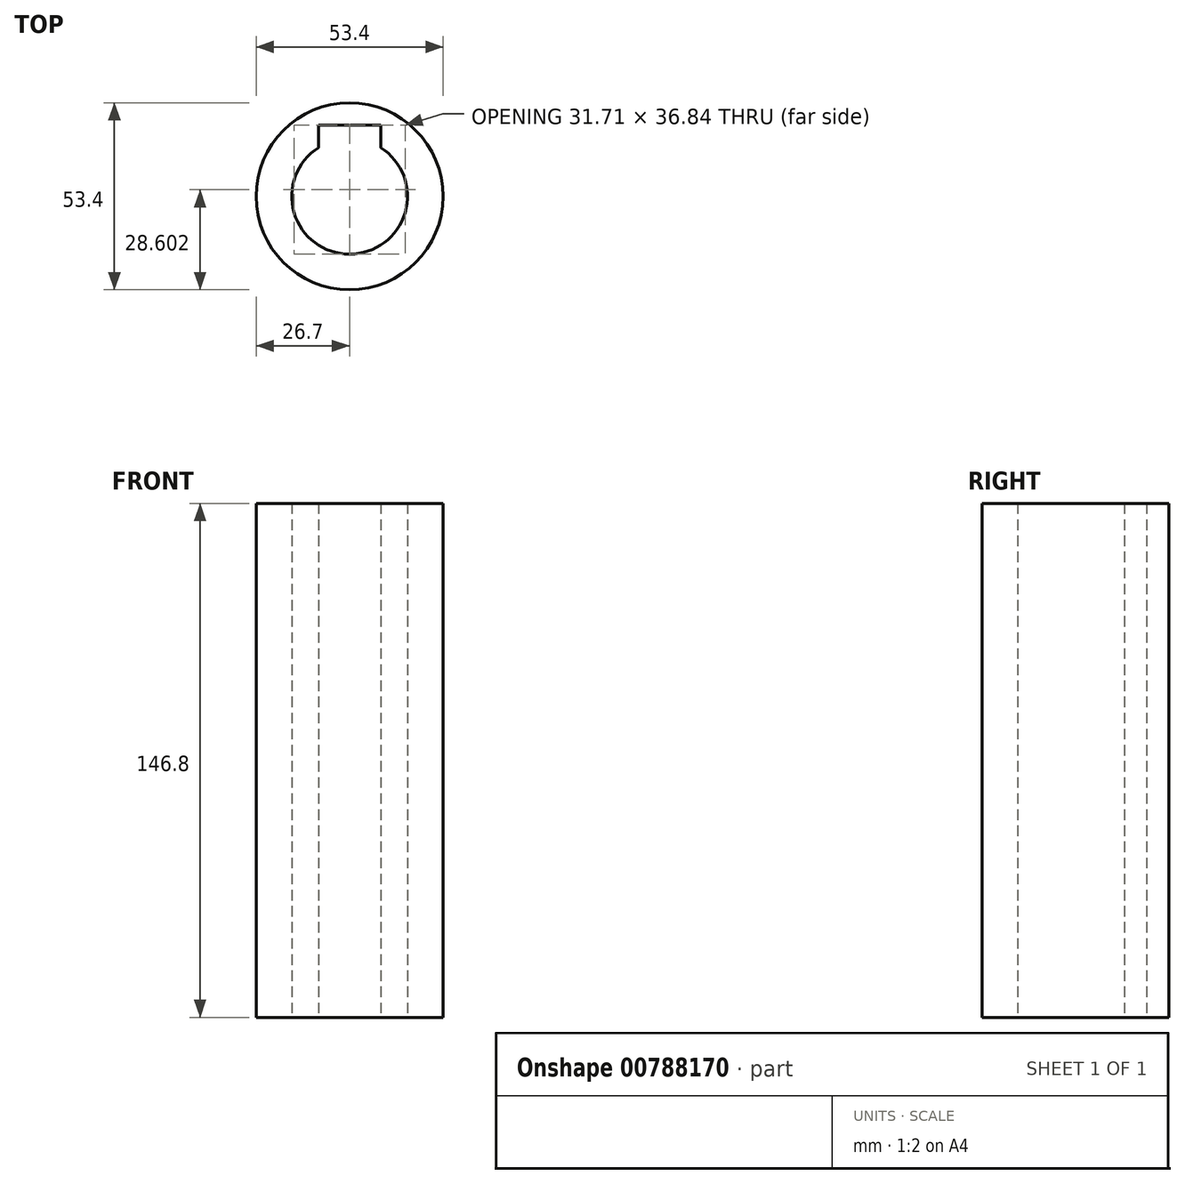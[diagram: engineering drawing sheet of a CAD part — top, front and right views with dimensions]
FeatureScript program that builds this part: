
annotation { "Feature Type Name" : "Feature", "Feature Type Description" : "" }
export const myFeature = defineFeature(function(context is Context, id is Id, definition is map)
    precondition{}
    {
        {
            var Q0;
            Q0=qCreatedBy(makeId("Top.planeOp"),FACE);
            var sketch = newSketch(context, id + "F0", { "sketchPlane" : qUnion([Q0])});
            skCircle(sketch, "E0", {"center": v(0, 0) * mm, "radius": 26.7 * mm});
            skCircle(sketch, "E1", {"center": v(0, 0) * mm, "radius": 16.52 * mm});
            skSolve(sketch);
        }
        {
            var Q0;
            Q0 = qSketchRegion(id + "F0", true);
            extrude(context, id + "F1", {"entities" : qUnion([Q0]), "depth" : 146.8 * mm, "offsetDistance" : 25.4 * mm});
        }
        {
            var Q0;
            Q0=makeQuery(id+"F1.opExtrude","CAP_FACE",FACE,{"disambiguationData":[OSD([sQuery(id+"F0.wireOp",EDGE,"E0"),sQuery(id+"F0.wireOp",EDGE,"E1")])],"isStart":true});
            var sketch = newSketch(context, id + "F2", { "sketchPlane" : qUnion([Q0])});
            skLineSegment(sketch, "E2", {"start": v(8.9, -20.32) * mm, "end": v(-8.9, -20.32) * mm});
            skLineSegment(sketch, "E3", {"start": v(-8.9, -20.32) * mm, "end": v(-8.9, 0) * mm});
            skLineSegment(sketch, "E4", {"start": v(-8.9, 0) * mm, "end": v(8.9, 0) * mm});
            skLineSegment(sketch, "E5", {"start": v(8.89, 0) * mm, "end": v(8.9, -20.32) * mm});
            skPoint(sketch, "E6.orphan", {"position": v(0, -66.6) * mm});
            skPoint(sketch, "E7.end.orphan", {"position": v(0, 0) * mm});
            skSolve(sketch);
        }
        {
            var Q0;
            {var subQ0=sQuery(id+"F2.wireOp",EDGE,"E2");Q0=makeQuery(id+"F2.imprint","IMPRINT",FACE,{"disambiguationData":[TD([[makeQuery(id+"F2.imprint","IMPRINT",EDGE,{"derivedFrom":subQ0}),-1.0]])]});}
            extrude(context, id + "F3", {"entities" : qUnion([Q0]), "operationType" : NewBodyOperationType.REMOVE, "endBound" : BoundingType.UP_TO_NEXT, "oppositeDirection" : true, "depth" : 25.4 * mm, "offsetDistance" : 25.4 * mm});
        }
    });
